# Revit family: Building-ElectricalVehicleCharging-GEWISS-JOINON-ION_WALL_MOUNTING
name_source: partatom
category: Apparecchi elettrici
units: mm (PartAtom-declared; Revit-internal decimal feet)

## family parameters
Condiviso = No
Host = Superficie
Mantenere orientamento annotazione = No
Punto di calcolo locali = No
Quota connettore circolare = Usa diametro
Taglio con vuoti quando caricato = No
Tipo di parte = Normale

## types (1)
- Building-ElectricalVehicleCharging-GEWISS-JOINON-ION_WALL_MOUNTING
    (Auto)restart electrical protections = Currently not present
    Charging activation = Remotely managed, via OCPP 1.6J
    Charging power = 22 kW + 2,3 kW
    Colour = Grey, Headboard RAL 7011
    Comunication = Ethernet Kit and 4G Modem with booster antenna
    Connectivity: = LAN,WIFI,4G
    Current supplied (max) = 32 A per socket (10 A for Type F)
    Customizations: = Yes (front)
    DC Leakage check = Currently not present
    Descrizione = WB JOINON RFID 22 kW 1xT2S+SC IP55 - 3G
    External treatments = Anti-corrosion and anti-graffiti
    Human Interface = LED RGB and TFT Display
    IDF = 47e6e16a-4526-4f48-a0f5-6d7f2c90a600
    INPUT: = -
    IP degree = IP54
    Immagine tipo = ION_PARETE.jpg
    Material = Steel sheet
    Mechanical characteristics = -
    Modello = GWJ2123W
    Mouting and installation = Wall mount
    N. of sockets Type 2 = 1 (+1 domestic socket Type F)
    OUTPUT : = -
    Operating temperature: = -25 +50 °C
    Power max. = 22 kW per socket (2,3 kW for type F)
    Power meter = YES (MID)
    Produttore = GEWISS S.p.A.
    Prospetto di default = 1219 mm
    Protection : = No
    RFID Reader = Yes
    Rated current: = 42 Ampere
    Rated insulation voltage (Ui) = 400 Volt
    Rated voltage = 400 Volt
    Shock resistance = IK10
    Simbolo in pianta = Sì
    Socket/Connector Nr. (Type) = 1 (Type 2 vandal-proof socket, with shutters) + 1 (Type F)
    Terminal blocks: = 1 x (5 x 10 mm²) + 1 x (3 x 6 mm²)
    Thermal-magnetic protection = Currently not present
    Total power: = 25 Chilowatt
    Type of residual current protection = Currently not present
    URL = https://www.gewiss.com
    Version file RFA = 19.4
